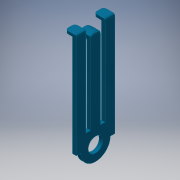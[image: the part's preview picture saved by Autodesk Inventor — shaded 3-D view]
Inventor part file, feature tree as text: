
AUTODESK INVENTOR PART (.ipt)
format: ipt  version: 2016 (Build 200138000, 138)  size: 382,976 bytes
history: native  units: in
note: dims shown in document units (in); Inventor stores cm internally (conversion verified against a paired STEP export)
features: extrude x14, sketch x14, reference x11, projected_geometry x9, fillet x6, plane x3
ambient origin geometry x8: Origin, YZ Plane, XZ Plane, XY Plane, X Axis, Y Axis, Z Axis, Center Point
bodies: Solid1 (feature_tree)
feature tree (57):
  extrude  "Extrusion1"  Depth=0.0079in
  sketch  "Sketch2"  dims[d12=0.052in d13=0.052in d14=0.052in]
  plane  "Work Plane1"
  plane  "Work Plane2"
  extrude  "Extrusion2"  Depth=0.052in
  fillet  "Fillet1"  Radius=0.052in
  extrude  "Extrusion3"  Depth=0.025in
  sketch  "Sketch4"  dims[d18=0.0197in d19=0.0in d20=0.0197in d21=0.0in]
  plane  "Work Plane3"
  extrude  "Extrusion4"  Depth=0.0197in TaperAngle=0.0deg
  extrude  "Extrusion5"  Depth=0.3937in TaperAngle=0.0deg
  fillet  "Fillet3"  Radius=0.0787in
  extrude  "Extrusion6"  Depth=0.0394in
  fillet  "Fillet5"  Radius=0.0394in
  fillet  "Fillet6"  Radius=0.1181in
  extrude  "Extrusion7"  Depth=0.052in
  fillet  "Fillet8"  Radius=0.052in
  extrude  "Extrusion8"  Depth=0.0039in
  fillet  "Fillet9"  Radius=0.0039in
  extrude  "Extrusion9"  Depth=0.0039in
  extrude  "Extrusion10"  Depth=1.0in TaperAngle=0.0deg
  extrude  "Extrusion11"  Depth=1.0in TaperAngle=0.0deg
  extrude  "Extrusion12"  Depth=1.0in TaperAngle=0.0deg
  extrude  "Extrusion13"  Depth=0.0394in TaperAngle=0.0deg
  extrude  "Extrusion14"  Depth=0.0394in TaperAngle=0.0deg
  sketch  "Sketch1"  dims[d9=0.0079in d11=0.0079in]
  reference  "Reference1"
  reference  "Reference2"
  reference  "Reference3"
  reference  "Reference4"
  reference  "Reference5"
  sketch  "Sketch3"  dims[d16=0.025in d17=0.025in]
  projected_geometry  "Projected Loop1"
  projected_geometry  "Projected Loop2"
  projected_geometry  "Projected Loop3"
  projected_geometry  "Projected Loop4"
  projected_geometry  "Projected Loop5"
  projected_geometry  "Projected Loop6"
  sketch  "Sketch5"  dims[d22=0.0197in d23=0.3937in d24=0.0in d25=0.0787in]
  reference  "Reference6"
  reference  "Reference7"
  reference  "Reference8"
  sketch  "Sketch6"  dims[d26=0.1969in d27=0.0in d29=0.0394in d30=0.0394in d31=0.1181in]
  reference  "Reference9"
  sketch  "Sketch7"  dims[d32=0.0394in d33=0.0in d34=0.0157in d36=0.052in]
  projected_geometry  "Projected Loop7"
  sketch  "Sketch8"  dims[d37=0.125in d38=0.0039in d39=0.0039in]
  sketch  "Sketch9"  dims[d40=1.0in d41=0.0in d42=0.0039in]
  sketch  "Sketch10"  dims[d43=0.0664in d45=1.0in d46=0.0in]
  sketch  "Sketch11"  dims[d47=0.0079in d48=1.0in d49=0.0in]
  projected_geometry  "Projected Loop8"
  sketch  "Sketch12"  dims[d50=0.4454in d51=1.0in d52=0.0in]
  reference  "Reference10"
  sketch  "Sketch13"  dims[d53=0.0394in d54=0.0in d55=0.0394in d56=0.0in]
  reference  "Reference11"
  sketch  "Sketch14"  dims[d58=0.0394in d59=0.0in d60=0.0394in d61=0.0in d62=0.0157in d63=0.0in]
  projected_geometry  "Projected Loop9"
